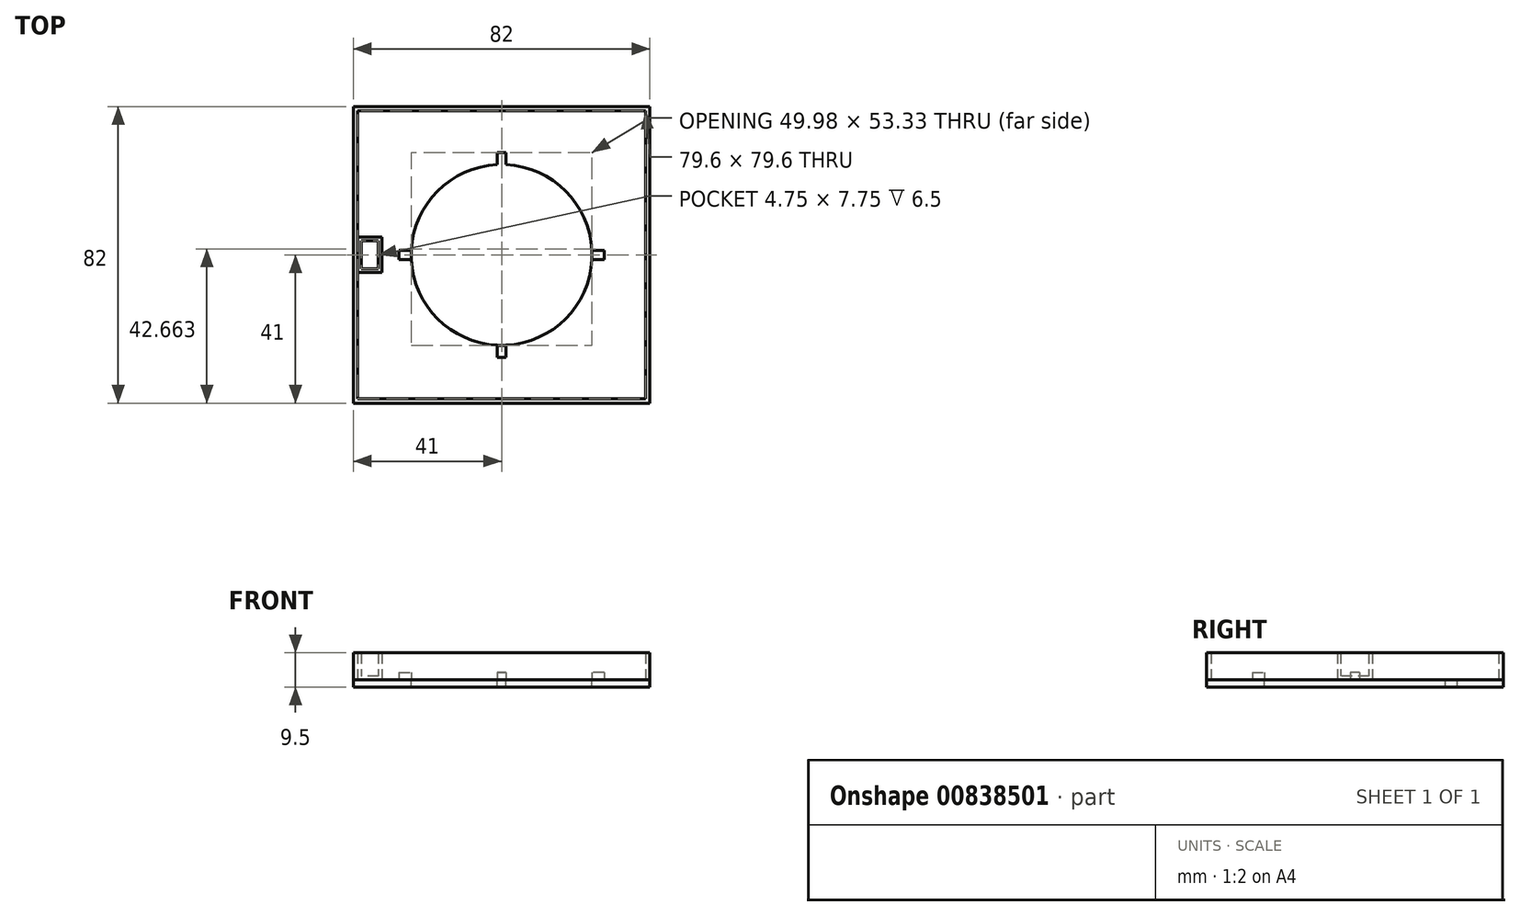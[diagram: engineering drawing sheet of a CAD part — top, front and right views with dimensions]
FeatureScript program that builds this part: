
annotation { "Feature Type Name" : "Feature", "Feature Type Description" : "" }
export const myFeature = defineFeature(function(context is Context, id is Id, definition is map)
    precondition{}
    {
        {
            var Q0;
            Q0=qCreatedBy(makeId("Top.planeOp"),FACE);
            var sketch = newSketch(context, id + "F0", { "sketchPlane" : qUnion([Q0])});
            skCircle(sketch, "E0", {"center": v(0, 0) * mm, "radius": 25 * mm});
            skCircle(sketch, "E1", {"center": v(0, 0) * mm, "radius": 32.8 * mm});
            skLineSegment(sketch, "E2.bottom", {"start": v(-1.25, 28.32) * mm, "end": v(1.25, 28.32) * mm});
            skLineSegment(sketch, "E2.top", {"start": v(-1.25, 21.68) * mm, "end": v(1.25, 21.68) * mm});
            skLineSegment(sketch, "E2.left", {"start": v(-1.25, 28.32) * mm, "end": v(-1.25, 21.68) * mm});
            skLineSegment(sketch, "E2.right", {"start": v(1.25, 28.32) * mm, "end": v(1.25, 21.68) * mm});
            skPoint(sketch, "E2.middle", {"position": v(0, 25) * mm});
            skLineSegment(sketch, "E3.bottom", {"start": v(28.33, 1.25) * mm, "end": v(21.68, 1.25) * mm});
            skLineSegment(sketch, "E3.top", {"start": v(28.33, -1.25) * mm, "end": v(21.68, -1.25) * mm});
            skLineSegment(sketch, "E3.left", {"start": v(28.33, 1.25) * mm, "end": v(28.33, -1.25) * mm});
            skLineSegment(sketch, "E3.right", {"start": v(21.68, 1.25) * mm, "end": v(21.68, -1.25) * mm});
            skPoint(sketch, "E3.middle", {"position": v(25, 0) * mm});
            skLineSegment(sketch, "E4.MirrorCS", {"start": v(1.25, 28.32) * mm, "end": v(-1.25, 28.32) * mm});
            skLineSegment(sketch, "E5.MirrorCS", {"start": v(1.25, 21.68) * mm, "end": v(-1.25, 21.68) * mm});
            skLineSegment(sketch, "E6.MirrorCS", {"start": v(-1.25, -21.68) * mm, "end": v(1.25, -21.68) * mm});
            skLineSegment(sketch, "E7.MirrorCS", {"start": v(-1.25, -28.32) * mm, "end": v(-1.25, -21.68) * mm});
            skLineSegment(sketch, "E8.MirrorCS", {"start": v(1.25, -28.32) * mm, "end": v(-1.25, -28.32) * mm});
            skLineSegment(sketch, "E9.MirrorCS", {"start": v(1.25, -28.32) * mm, "end": v(1.25, -21.68) * mm});
            skLineSegment(sketch, "E10.MirrorCS", {"start": v(-21.68, 1.25) * mm, "end": v(-21.68, -1.25) * mm});
            skLineSegment(sketch, "E11.MirrorCS", {"start": v(-28.33, 1.25) * mm, "end": v(-21.68, 1.25) * mm});
            skLineSegment(sketch, "E12.MirrorCS", {"start": v(-28.33, -1.25) * mm, "end": v(-21.68, -1.25) * mm});
            skLineSegment(sketch, "E13.MirrorCS", {"start": v(-28.33, 1.25) * mm, "end": v(-28.33, -1.25) * mm});
            skPoint(sketch, "E14.middle", {"position": v(-41.79, 0) * mm});
            skCircle(sketch, "E15", {"center": v(0, 0) * mm, "radius": 23.8 * mm});
            skLineSegment(sketch, "E16.bottom", {"start": v(-39.8, 39.8) * mm, "end": v(39.8, 39.8) * mm});
            skLineSegment(sketch, "E16.top", {"start": v(-39.8, -39.8) * mm, "end": v(39.8, -39.8) * mm});
            skLineSegment(sketch, "E16.left", {"start": v(-39.8, 39.8) * mm, "end": v(-39.8, -39.8) * mm});
            skLineSegment(sketch, "E16.right", {"start": v(39.8, 39.8) * mm, "end": v(39.8, -39.8) * mm});
            skLineSegment(sketch, "E17.bottom", {"start": v(-41, 41) * mm, "end": v(41, 41) * mm});
            skLineSegment(sketch, "E17.top", {"start": v(-41, -41) * mm, "end": v(41, -41) * mm});
            skLineSegment(sketch, "E17.left", {"start": v(-41, 41) * mm, "end": v(-41, -41) * mm});
            skLineSegment(sketch, "E17.right", {"start": v(41, 41) * mm, "end": v(41, -41) * mm});
            skLineSegment(sketch, "E18.bottom", {"start": v(-33.05, -4.87) * mm, "end": v(-39.8, -4.87) * mm});
            skLineSegment(sketch, "E18.top", {"start": v(-33.05, 4.88) * mm, "end": v(-39.8, 4.88) * mm});
            skLineSegment(sketch, "E18.left", {"start": v(-33.05, -4.87) * mm, "end": v(-33.05, 4.88) * mm});
            skLineSegment(sketch, "E18.right", {"start": v(-39.8, -4.87) * mm, "end": v(-39.8, 4.88) * mm});
            skPoint(sketch, "E18.middle", {"position": v(-36.42, 0) * mm});
            skSolve(sketch);
        }
        {
            var Q0;
            {var subQ0=sQuery(id+"F0.wireOp",EDGE,"E14.top");var subQ1=sQuery(id+"F0.wireOp",EDGE,"ETdMOg9K-giOR-L7Ai-rbHK-IAAoiEiWwUd0");var subQ2=makeQuery(id+"F0.imprint","INTERSECT",VERTEX,{"derivedFrom":[subQ1,subQ0]});Q0=makeQuery(id+"F0.imprint","IMPRINT",FACE,{"disambiguationData":[TD([[makeQuery(id+"F0.imprint","IMPRINT",EDGE,{"disambiguationData":[TD([[subQ2,1.0]])],"derivedFrom":subQ1}),-1.0]])]});}
            var Q1;
            {var subQ3=sQuery(id+"F0.wireOp",EDGE,"ETdMOg9K-giOR-L7Ai-rbHK-IAAoiEiWwUd0");var subQ5=makeQuery(id+"F0.imprint","INTERSECT",VERTEX,{"derivedFrom":[subQ3,sQuery(id+"F0.wireOp",EDGE,"7CK1xZji-ef6t-rpsp-r9yB-K5cPyd019NKb")]});Q1=makeQuery(id+"F0.imprint","IMPRINT",FACE,{"disambiguationData":[TD([[makeQuery(id+"F0.imprint","IMPRINT",EDGE,{"disambiguationData":[TD([[subQ5,1.0]])],"derivedFrom":subQ3}),-1.0]])]});}
            var Q2;
            {var subQ0=sQuery(id+"F0.wireOp",EDGE,"E7.MirrorCS");var subQ1=sQuery(id+"F0.wireOp",EDGE,"E0");var subQ2=makeQuery(id+"F0.imprint","INTERSECT",VERTEX,{"derivedFrom":[subQ1,subQ0]});Q2=makeQuery(id+"F0.imprint","IMPRINT",FACE,{"disambiguationData":[TD([[makeQuery(id+"F0.imprint","IMPRINT",EDGE,{"disambiguationData":[TD([[subQ2,-1.0]])],"derivedFrom":subQ1}),-1.0]])]});}
            var Q3;
            {var subQ0=sQuery(id+"F0.wireOp",EDGE,"E11.MirrorCS");var subQ1=sQuery(id+"F0.wireOp",EDGE,"E0");var subQ2=makeQuery(id+"F0.imprint","INTERSECT",VERTEX,{"derivedFrom":[subQ1,subQ0]});Q3=makeQuery(id+"F0.imprint","IMPRINT",FACE,{"disambiguationData":[TD([[makeQuery(id+"F0.imprint","IMPRINT",EDGE,{"disambiguationData":[TD([[subQ2,-1.0]])],"derivedFrom":subQ1}),-1.0]])]});}
            var Q4;
            {var subQ0=sQuery(id+"F0.wireOp",EDGE,"E2.right");var subQ1=sQuery(id+"F0.wireOp",EDGE,"E0");var subQ2=makeQuery(id+"F0.imprint","INTERSECT",VERTEX,{"derivedFrom":[subQ1,subQ0]});Q4=makeQuery(id+"F0.imprint","IMPRINT",FACE,{"disambiguationData":[TD([[makeQuery(id+"F0.imprint","IMPRINT",EDGE,{"disambiguationData":[TD([[subQ2,-1.0]])],"derivedFrom":subQ1}),-1.0]])]});}
            var Q5;
            {var subQ0=sQuery(id+"F0.wireOp",EDGE,"E9.MirrorCS");var subQ1=sQuery(id+"F0.wireOp",EDGE,"E0");var subQ2=makeQuery(id+"F0.imprint","INTERSECT",VERTEX,{"derivedFrom":[subQ1,subQ0]});Q5=makeQuery(id+"F0.imprint","IMPRINT",FACE,{"disambiguationData":[TD([[makeQuery(id+"F0.imprint","IMPRINT",EDGE,{"disambiguationData":[TD([[subQ2,1.0]])],"derivedFrom":subQ1}),-1.0]])]});}
            var Q6;
            {var subQ0=sQuery(id+"F0.wireOp",EDGE,"E2.left");var subQ1=sQuery(id+"F0.wireOp",EDGE,"E0");var subQ2=makeQuery(id+"F0.imprint","INTERSECT",VERTEX,{"derivedFrom":[subQ1,subQ0]});Q6=makeQuery(id+"F0.imprint","IMPRINT",FACE,{"disambiguationData":[TD([[makeQuery(id+"F0.imprint","IMPRINT",EDGE,{"disambiguationData":[TD([[subQ2,-1.0]])],"derivedFrom":subQ1}),-1.0]])]});}
            var Q7;
            {var subQ0=sQuery(id+"F0.wireOp",EDGE,"E9.MirrorCS");var subQ1=sQuery(id+"F0.wireOp",EDGE,"E0");var subQ2=makeQuery(id+"F0.imprint","INTERSECT",VERTEX,{"derivedFrom":[subQ1,subQ0]});Q7=makeQuery(id+"F0.imprint","IMPRINT",FACE,{"disambiguationData":[TD([[makeQuery(id+"F0.imprint","IMPRINT",EDGE,{"disambiguationData":[TD([[subQ2,-1.0]])],"derivedFrom":subQ1}),-1.0]])]});}
            var Q8;
            {var subQ0=sQuery(id+"F0.wireOp",EDGE,"E3.top");var subQ1=sQuery(id+"F0.wireOp",EDGE,"E0");var subQ2=makeQuery(id+"F0.imprint","INTERSECT",VERTEX,{"derivedFrom":[subQ1,subQ0]});Q8=makeQuery(id+"F0.imprint","IMPRINT",FACE,{"disambiguationData":[TD([[makeQuery(id+"F0.imprint","IMPRINT",EDGE,{"disambiguationData":[TD([[subQ2,1.0]])],"derivedFrom":subQ1}),-1.0]])]});}
            var Q9;
            {var subQ0=sQuery(id+"F0.wireOp",EDGE,"E12.MirrorCS");var subQ1=sQuery(id+"F0.wireOp",EDGE,"E0");var subQ2=makeQuery(id+"F0.imprint","INTERSECT",VERTEX,{"derivedFrom":[subQ1,subQ0]});Q9=makeQuery(id+"F0.imprint","IMPRINT",FACE,{"disambiguationData":[TD([[makeQuery(id+"F0.imprint","IMPRINT",EDGE,{"disambiguationData":[TD([[subQ2,-1.0]])],"derivedFrom":subQ1}),-1.0]])]});}
            var Q10;
            Q10=makeQuery(id+"F0.imprint","IMPRINT",FACE,{"disambiguationData":[TD([[makeQuery(id+"F0.imprint","IMPRINT",EDGE,{"derivedFrom":sQuery(id+"F0.wireOp",EDGE,"E16.bottom")}),1.0]])]});
            var Q11;
            Q11=sQuery(id+"F0.wireOp",EDGE,"ETdMOg9K-giOR-L7Ai-rbHK-IAAoiEiWwUd0");
            var Q12;
            Q12=sQuery(id+"F0.wireOp",EDGE,"E0");
            extrude(context, id + "F1", {"entities" : qUnion([Q0, Q1, Q2, Q3, Q4, Q5, Q6, Q7, Q8, Q9, Q10]), "surfaceEntities" : qUnion([Q11, Q12]), "depth" : 7.5 * mm, "offsetDistance" : 25 * mm});
        }
        {
            var Q0;
            Q0=makeQuery(id+"F0.imprint","IMPRINT",FACE,{"disambiguationData":[TD([[makeQuery(id+"F0.imprint","IMPRINT",EDGE,{"derivedFrom":sQuery(id+"F0.wireOp",EDGE,"E1")}),-1.0]])]});
            var Q1;
            Q1=makeQuery(id+"F0.imprint","IMPRINT",FACE,{"disambiguationData":[TD([[makeQuery(id+"F0.imprint","IMPRINT",EDGE,{"derivedFrom":sQuery(id+"F0.wireOp",EDGE,"E0")}),-1.0]])]});
            var Q2;
            Q2=makeQuery(id+"F0.imprint","IMPRINT",FACE,{"disambiguationData":[TD([[makeQuery(id+"F0.imprint","IMPRINT",EDGE,{"derivedFrom":sQuery(id+"F0.wireOp",EDGE,"7CK1xZji-ef6t-rpsp-r9yB-K5cPyd019NKb")}),1.0]])]});
            var Q3;
            Q3=makeQuery(id+"F0.imprint","IMPRINT",FACE,{"disambiguationData":[TD([[makeQuery(id+"F0.imprint","IMPRINT",EDGE,{"derivedFrom":sQuery(id+"F0.wireOp",EDGE,"E1")}),1.0]])]});
            var Q4;
            {var subQ5=sQuery(id+"F0.wireOp",EDGE,"E13.MirrorCS");Q4=makeQuery(id+"F0.imprint","IMPRINT",FACE,{"disambiguationData":[TD([[makeQuery(id+"F0.imprint","IMPRINT",EDGE,{"derivedFrom":subQ5}),1.0]])]});}
            var Q5;
            {var subQ5=sQuery(id+"F0.wireOp",EDGE,"E8.MirrorCS");Q5=makeQuery(id+"F0.imprint","IMPRINT",FACE,{"disambiguationData":[TD([[makeQuery(id+"F0.imprint","IMPRINT",EDGE,{"derivedFrom":subQ5}),-1.0]])]});}
            var Q6;
            {var subQ5=sQuery(id+"F0.wireOp",EDGE,"E4.MirrorCS");Q6=makeQuery(id+"F0.imprint","IMPRINT",FACE,{"disambiguationData":[TD([[makeQuery(id+"F0.imprint","IMPRINT",EDGE,{"derivedFrom":subQ5}),1.0]])]});}
            var Q7;
            {var subQ5=sQuery(id+"F0.wireOp",EDGE,"E3.left");Q7=makeQuery(id+"F0.imprint","IMPRINT",FACE,{"disambiguationData":[TD([[makeQuery(id+"F0.imprint","IMPRINT",EDGE,{"derivedFrom":subQ5}),-1.0]])]});}
            var Q8;
            {var subQ0=sQuery(id+"F0.wireOp",EDGE,"E14.top");var subQ1=sQuery(id+"F0.wireOp",EDGE,"ETdMOg9K-giOR-L7Ai-rbHK-IAAoiEiWwUd0");var subQ2=makeQuery(id+"F0.imprint","INTERSECT",VERTEX,{"derivedFrom":[subQ1,subQ0]});Q8=makeQuery(id+"F0.imprint","IMPRINT",FACE,{"disambiguationData":[TD([[makeQuery(id+"F0.imprint","IMPRINT",EDGE,{"disambiguationData":[TD([[subQ2,1.0]])],"derivedFrom":subQ1}),-1.0]])]});}
            var Q9;
            {var subQ1=sQuery(id+"F0.wireOp",EDGE,"aaf08cbb-e0e6-44e5-a82d-b8a05a9542510.MirrorCS");Q9=makeQuery(id+"F0.imprint","IMPRINT",FACE,{"disambiguationData":[TD([[makeQuery(id+"F0.imprint","IMPRINT",EDGE,{"derivedFrom":subQ1}),1.0]])]});}
            var Q10;
            {var subQ0=sQuery(id+"F0.wireOp",EDGE,"SpKwcO3M-pOnQ-yAnI-ckbO-jszkQa1rbotf.top");Q10=makeQuery(id+"F0.imprint","IMPRINT",FACE,{"disambiguationData":[TD([[makeQuery(id+"F0.imprint","IMPRINT",EDGE,{"derivedFrom":subQ0}),-1.0]])]});}
            var Q11;
            {var subQ1=sQuery(id+"F0.wireOp",EDGE,"SpKwcO3M-pOnQ-yAnI-ckbO-jszkQa1rbotf.bottom");Q11=makeQuery(id+"F0.imprint","IMPRINT",FACE,{"disambiguationData":[TD([[makeQuery(id+"F0.imprint","IMPRINT",EDGE,{"derivedFrom":subQ1}),1.0]])]});}
            var Q12;
            {var subQ0=sQuery(id+"F0.wireOp",EDGE,"7CK1xZji-ef6t-rpsp-r9yB-K5cPyd019NKb");var subQ1=sQuery(id+"F0.wireOp",EDGE,"ETdMOg9K-giOR-L7Ai-rbHK-IAAoiEiWwUd0");var subQ2=makeQuery(id+"F0.imprint","INTERSECT",VERTEX,{"derivedFrom":[subQ1,subQ0]});Q12=makeQuery(id+"F0.imprint","IMPRINT",FACE,{"disambiguationData":[TD([[makeQuery(id+"F0.imprint","IMPRINT",EDGE,{"disambiguationData":[TD([[subQ2,-1.0]])],"derivedFrom":subQ1}),1.0]])]});}
            var Q13;
            {var subQ0=sQuery(id+"F0.wireOp",EDGE,"7CK1xZji-ef6t-rpsp-r9yB-K5cPyd019NKb");var subQ1=sQuery(id+"F0.wireOp",EDGE,"ETdMOg9K-giOR-L7Ai-rbHK-IAAoiEiWwUd0");var subQ2=makeQuery(id+"F0.imprint","INTERSECT",VERTEX,{"derivedFrom":[subQ1,subQ0]});Q13=makeQuery(id+"F0.imprint","IMPRINT",FACE,{"disambiguationData":[TD([[makeQuery(id+"F0.imprint","IMPRINT",EDGE,{"disambiguationData":[TD([[subQ2,1.0]])],"derivedFrom":subQ1}),1.0]])]});}
            var Q14;
            {var subQ0=sQuery(id+"F0.wireOp",EDGE,"7e1316c8-d3c2-4bb1-b3af-9022fed48cfa0.MirrorCS");Q14=makeQuery(id+"F0.imprint","IMPRINT",FACE,{"disambiguationData":[TD([[makeQuery(id+"F0.imprint","IMPRINT",EDGE,{"derivedFrom":subQ0}),-1.0]])]});}
            var Q15;
            {var subQ3=sQuery(id+"F0.wireOp",EDGE,"ETdMOg9K-giOR-L7Ai-rbHK-IAAoiEiWwUd0");var subQ8=makeQuery(id+"F0.imprint","INTERSECT",VERTEX,{"derivedFrom":[subQ3,sQuery(id+"F0.wireOp",EDGE,"7CK1xZji-ef6t-rpsp-r9yB-K5cPyd019NKb")]});Q15=makeQuery(id+"F0.imprint","IMPRINT",FACE,{"disambiguationData":[TD([[makeQuery(id+"F0.imprint","IMPRINT",EDGE,{"disambiguationData":[TD([[subQ8,1.0]])],"derivedFrom":subQ3}),-1.0]])]});}
            var Q16;
            {var subQ1=sQuery(id+"F0.wireOp",EDGE,"aaf08cbb-e0e6-44e5-a82d-b8a05a9542510.MirrorCS");Q16=makeQuery(id+"F0.imprint","IMPRINT",FACE,{"disambiguationData":[TD([[makeQuery(id+"F0.imprint","IMPRINT",EDGE,{"derivedFrom":subQ1}),1.0]])]});}
            var Q17;
            Q17=makeQuery(id+"F0.imprint","IMPRINT",FACE,{"disambiguationData":[TD([[makeQuery(id+"F0.imprint","IMPRINT",EDGE,{"derivedFrom":sQuery(id+"F0.wireOp",EDGE,"E1")}),-1.0]])]});
            var Q18;
            {var subQ0=sQuery(id+"F0.wireOp",EDGE,"SpKwcO3M-pOnQ-yAnI-ckbO-jszkQa1rbotf.right");var subQ1=sQuery(id+"F0.wireOp",EDGE,"7CK1xZji-ef6t-rpsp-r9yB-K5cPyd019NKb");var subQ2=makeQuery(id+"F0.imprint","INTERSECT",VERTEX,{"derivedFrom":[subQ1,subQ0]});Q18=makeQuery(id+"F0.imprint","IMPRINT",FACE,{"disambiguationData":[TD([[makeQuery(id+"F0.imprint","IMPRINT",EDGE,{"disambiguationData":[TD([[subQ2,1.0]])],"derivedFrom":subQ1}),1.0]])]});}
            var Q19;
            {var subQ1=sQuery(id+"F0.wireOp",EDGE,"SpKwcO3M-pOnQ-yAnI-ckbO-jszkQa1rbotf.bottom");Q19=makeQuery(id+"F0.imprint","IMPRINT",FACE,{"disambiguationData":[TD([[makeQuery(id+"F0.imprint","IMPRINT",EDGE,{"derivedFrom":subQ1}),-1.0]])]});}
            var Q20;
            Q20=makeQuery(id+"F0.imprint","IMPRINT",FACE,{"disambiguationData":[TD([[makeQuery(id+"F0.imprint","IMPRINT",EDGE,{"derivedFrom":sQuery(id+"F0.wireOp",EDGE,"E16.bottom")}),1.0]])]});
            var Q21;
            Q21=makeQuery(id+"F0.imprint","IMPRINT",FACE,{"disambiguationData":[TD([[makeQuery(id+"F0.imprint","IMPRINT",EDGE,{"derivedFrom":sQuery(id+"F0.wireOp",EDGE,"E18.bottom")}),-1.0]])]});
            var Q22;
            {var subQ0=sQuery(id+"F0.wireOp",EDGE,"E11.MirrorCS");var subQ1=sQuery(id+"F0.wireOp",EDGE,"E0");var subQ2=makeQuery(id+"F0.imprint","INTERSECT",VERTEX,{"derivedFrom":[subQ1,subQ0]});Q22=makeQuery(id+"F0.imprint","IMPRINT",FACE,{"disambiguationData":[TD([[makeQuery(id+"F0.imprint","IMPRINT",EDGE,{"disambiguationData":[TD([[subQ2,-1.0]])],"derivedFrom":subQ1}),-1.0]])]});}
            var Q23;
            {var subQ0=sQuery(id+"F0.wireOp",EDGE,"E2.right");var subQ1=sQuery(id+"F0.wireOp",EDGE,"E0");var subQ2=makeQuery(id+"F0.imprint","INTERSECT",VERTEX,{"derivedFrom":[subQ1,subQ0]});Q23=makeQuery(id+"F0.imprint","IMPRINT",FACE,{"disambiguationData":[TD([[makeQuery(id+"F0.imprint","IMPRINT",EDGE,{"disambiguationData":[TD([[subQ2,-1.0]])],"derivedFrom":subQ1}),-1.0]])]});}
            var Q24;
            {var subQ0=sQuery(id+"F0.wireOp",EDGE,"E2.left");var subQ1=sQuery(id+"F0.wireOp",EDGE,"E0");var subQ2=makeQuery(id+"F0.imprint","INTERSECT",VERTEX,{"derivedFrom":[subQ1,subQ0]});Q24=makeQuery(id+"F0.imprint","IMPRINT",FACE,{"disambiguationData":[TD([[makeQuery(id+"F0.imprint","IMPRINT",EDGE,{"disambiguationData":[TD([[subQ2,-1.0]])],"derivedFrom":subQ1}),-1.0]])]});}
            var Q25;
            {var subQ0=sQuery(id+"F0.wireOp",EDGE,"E3.top");var subQ1=sQuery(id+"F0.wireOp",EDGE,"E0");var subQ2=makeQuery(id+"F0.imprint","INTERSECT",VERTEX,{"derivedFrom":[subQ1,subQ0]});Q25=makeQuery(id+"F0.imprint","IMPRINT",FACE,{"disambiguationData":[TD([[makeQuery(id+"F0.imprint","IMPRINT",EDGE,{"disambiguationData":[TD([[subQ2,1.0]])],"derivedFrom":subQ1}),-1.0]])]});}
            var Q26;
            {var subQ0=sQuery(id+"F0.wireOp",EDGE,"E9.MirrorCS");var subQ1=sQuery(id+"F0.wireOp",EDGE,"E0");var subQ2=makeQuery(id+"F0.imprint","INTERSECT",VERTEX,{"derivedFrom":[subQ1,subQ0]});Q26=makeQuery(id+"F0.imprint","IMPRINT",FACE,{"disambiguationData":[TD([[makeQuery(id+"F0.imprint","IMPRINT",EDGE,{"disambiguationData":[TD([[subQ2,1.0]])],"derivedFrom":subQ1}),-1.0]])]});}
            var Q27;
            {var subQ0=sQuery(id+"F0.wireOp",EDGE,"E12.MirrorCS");var subQ1=sQuery(id+"F0.wireOp",EDGE,"E0");var subQ2=makeQuery(id+"F0.imprint","INTERSECT",VERTEX,{"derivedFrom":[subQ1,subQ0]});Q27=makeQuery(id+"F0.imprint","IMPRINT",FACE,{"disambiguationData":[TD([[makeQuery(id+"F0.imprint","IMPRINT",EDGE,{"disambiguationData":[TD([[subQ2,-1.0]])],"derivedFrom":subQ1}),-1.0]])]});}
            var Q28;
            {var subQ0=sQuery(id+"F0.wireOp",EDGE,"E7.MirrorCS");var subQ1=sQuery(id+"F0.wireOp",EDGE,"E0");var subQ2=makeQuery(id+"F0.imprint","INTERSECT",VERTEX,{"derivedFrom":[subQ1,subQ0]});Q28=makeQuery(id+"F0.imprint","IMPRINT",FACE,{"disambiguationData":[TD([[makeQuery(id+"F0.imprint","IMPRINT",EDGE,{"disambiguationData":[TD([[subQ2,-1.0]])],"derivedFrom":subQ1}),-1.0]])]});}
            var Q29;
            {var subQ0=sQuery(id+"F0.wireOp",EDGE,"E9.MirrorCS");var subQ1=sQuery(id+"F0.wireOp",EDGE,"E0");var subQ2=makeQuery(id+"F0.imprint","INTERSECT",VERTEX,{"derivedFrom":[subQ1,subQ0]});Q29=makeQuery(id+"F0.imprint","IMPRINT",FACE,{"disambiguationData":[TD([[makeQuery(id+"F0.imprint","IMPRINT",EDGE,{"disambiguationData":[TD([[subQ2,-1.0]])],"derivedFrom":subQ1}),-1.0]])]});}
            var Q30;
            Q30=sQuery(id+"F0.wireOp",EDGE,"ETdMOg9K-giOR-L7Ai-rbHK-IAAoiEiWwUd0");
            var Q31;
            Q31=sQuery(id+"F0.wireOp",EDGE,"E0");
            extrude(context, id + "F2", {"entities" : qUnion([Q0, Q1, Q2, Q3, Q4, Q5, Q6, Q7, Q8, Q9, Q10, Q11, Q12, Q13, Q14, Q15, Q16, Q17, Q18, Q19, Q20, Q21, Q22, Q23, Q24, Q25, Q26, Q27, Q28, Q29]), "surfaceOperationType" : NewSurfaceOperationType.ADD, "surfaceEntities" : qUnion([Q30, Q31]), "oppositeDirection" : true, "depth" : 2 * mm, "offsetDistance" : 25 * mm});
        }
        {
            var Q0;
            {var subQ5=sQuery(id+"F0.wireOp",EDGE,"E13.MirrorCS");Q0=makeQuery(id+"F0.imprint","IMPRINT",FACE,{"disambiguationData":[TD([[makeQuery(id+"F0.imprint","IMPRINT",EDGE,{"derivedFrom":subQ5}),1.0]])]});}
            var Q1;
            {var subQ5=sQuery(id+"F0.wireOp",EDGE,"E4.MirrorCS");Q1=makeQuery(id+"F0.imprint","IMPRINT",FACE,{"disambiguationData":[TD([[makeQuery(id+"F0.imprint","IMPRINT",EDGE,{"derivedFrom":subQ5}),1.0]])]});}
            var Q2;
            {var subQ5=sQuery(id+"F0.wireOp",EDGE,"E3.left");Q2=makeQuery(id+"F0.imprint","IMPRINT",FACE,{"disambiguationData":[TD([[makeQuery(id+"F0.imprint","IMPRINT",EDGE,{"derivedFrom":subQ5}),-1.0]])]});}
            var Q3;
            {var subQ5=sQuery(id+"F0.wireOp",EDGE,"E8.MirrorCS");Q3=makeQuery(id+"F0.imprint","IMPRINT",FACE,{"disambiguationData":[TD([[makeQuery(id+"F0.imprint","IMPRINT",EDGE,{"derivedFrom":subQ5}),-1.0]])]});}
            extrude(context, id + "F3", {"entities" : qUnion([Q0, Q1, Q2, Q3]), "depth" : 2 * mm, "offsetDistance" : 25 * mm});
        }
        {
            var Q0;
            Q0=makeQuery(id+"F0.imprint","IMPRINT",FACE,{"disambiguationData":[TD([[makeQuery(id+"F0.imprint","IMPRINT",EDGE,{"derivedFrom":sQuery(id+"F0.wireOp",EDGE,"E18.bottom")}),-1.0]])]});
            extrude(context, id + "F4", {"entities" : qUnion([Q0]), "depth" : 7.5 * mm, "offsetDistance" : 25 * mm});
        }
        {
            var Q0;
            Q0=makeQuery(id+"F4.opExtrude","SWEPT_FACE",FACE,{"disambiguationData":[OSD([sQuery(id+"F0.wireOp",EDGE,"E18.right")])]});
            var Q1;
            Q1=makeQuery(id+"F4.opExtrude","CAP_FACE",FACE,{"disambiguationData":[OSD([sQuery(id+"F0.wireOp",EDGE,"E18.bottom"),sQuery(id+"F0.wireOp",EDGE,"E18.top"),sQuery(id+"F0.wireOp",EDGE,"E18.left"),sQuery(id+"F0.wireOp",EDGE,"E18.right")])],"isStart":false});
            shell(context, id + "F5", {"entities" : qUnion([Q0, Q1]), "thickness" : 1 * mm});
        }
    });
